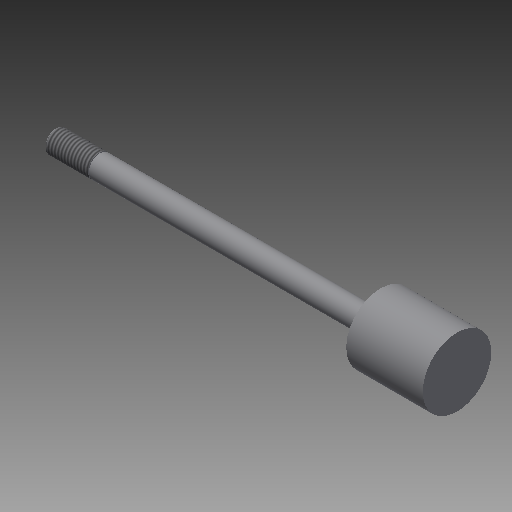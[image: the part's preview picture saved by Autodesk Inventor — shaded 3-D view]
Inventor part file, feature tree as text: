
AUTODESK INVENTOR PART (.ipt)
format: ipt  version: 2019 (Build 230136000, 136)  size: 162,304 bytes
history: native  units: in
note: dims shown in document units (in); Inventor stores cm internally (conversion verified against a paired STEP export)
features: other x84, revolve x3, sketch x3, thread x1
ambient origin geometry x8: Origin, YZ Plane, XZ Plane, XY Plane, X Axis, Y Axis, Z Axis, Center Point
bodies: Solid1 (feature_tree)
feature tree (91):
  revolve  "Revolution1"  Angle=360.0deg
  revolve  "Revolution2"  Angle=360.0deg
  thread  "Thread1"  [1 undecoded]
  revolve  "Revolution3"  [1 undecoded]
  other  "dia1_XY"
  other  "dia1_YZ"
  other  "dia1_ZX"
  other  "dia1_X"
  other  "dia1_Y"
  other  "dia1_Z"
  other  "dia1_Center"
  other  "dia12_XY"
  other  "dia12_YZ"
  other  "dia12_ZX"
  other  "dia12_X"
  other  "dia12_Y"
  other  "dia12_Z"
  other  "dia12_Center"
  other  "dia2_XY"
  other  "dia2_YZ"
  other  "dia2_ZX"
  other  "dia2_X"
  other  "dia2_Y"
  other  "dia2_Z"
  other  "dia2_Center"
  other  "dia22_XY"
  other  "dia22_YZ"
  other  "dia22_ZX"
  other  "dia22_X"
  other  "dia22_Y"
  other  "dia22_Z"
  other  "dia22_Center"
  other  "hh1_XY"
  other  "hh1_YZ"
  other  "hh1_ZX"
  other  "hh1_X"
  other  "hh1_Y"
  other  "hh1_Z"
  other  "hh1_Center"
  other  "hh2_XY"
  other  "hh2_YZ"
  other  "hh2_ZX"
  other  "hh2_X"
  other  "hh2_Y"
  other  "hh2_Z"
  other  "hh2_Center"
  other  "rl1_XY"
  other  "rl1_YZ"
  other  "rl1_ZX"
  other  "rl1_X"
  other  "rl1_Y"
  other  "rl1_Z"
  other  "rl1_Center"
  other  "rl2_XY"
  other  "rl2_YZ"
  other  "rl2_ZX"
  other  "rl2_X"
  other  "rl2_Y"
  other  "rl2_Z"
  other  "rl2_Center"
  other  "rod_cp_XY"
  other  "rod_cp_YZ"
  other  "rod_cp_ZX"
  other  "rod_cp_X"
  other  "rod_cp_Y"
  other  "rod_cp_Z"
  other  "rod_cp_Center"
  other  "thd1_XY"
  other  "thd1_YZ"
  other  "thd1_ZX"
  other  "thd1_X"
  other  "thd1_Y"
  other  "thd1_Z"
  other  "thd1_Center"
  other  "thd2_XY"
  other  "thd2_YZ"
  other  "thd2_ZX"
  other  "thd2_X"
  other  "thd2_Y"
  other  "thd2_Z"
  other  "thd2_Center"
  other  "to_rod_clevis_XY"
  other  "to_rod_clevis_YZ"
  other  "to_rod_clevis_ZX"
  other  "to_rod_clevis_X"
  other  "to_rod_clevis_Y"
  other  "to_rod_clevis_Z"
  other  "to_rod_clevis_Center"
  sketch  "Sketch_1"  dims[d0=360.0deg d1=360.0deg]
  sketch  "Sketch_3"  dims[d2=0.4787in d3=0.0in d4=360.0deg]
  sketch  "Sketch_30"  dims[d5=0.0in d6=0.0in d7=0.0in d8=0.0in d9=0.0in]
note: 2 required parameter values undecoded (feature->parameter linkage not recoverable at this tier; creation-order binding heuristic only, values carry confidence <= 0.55)
